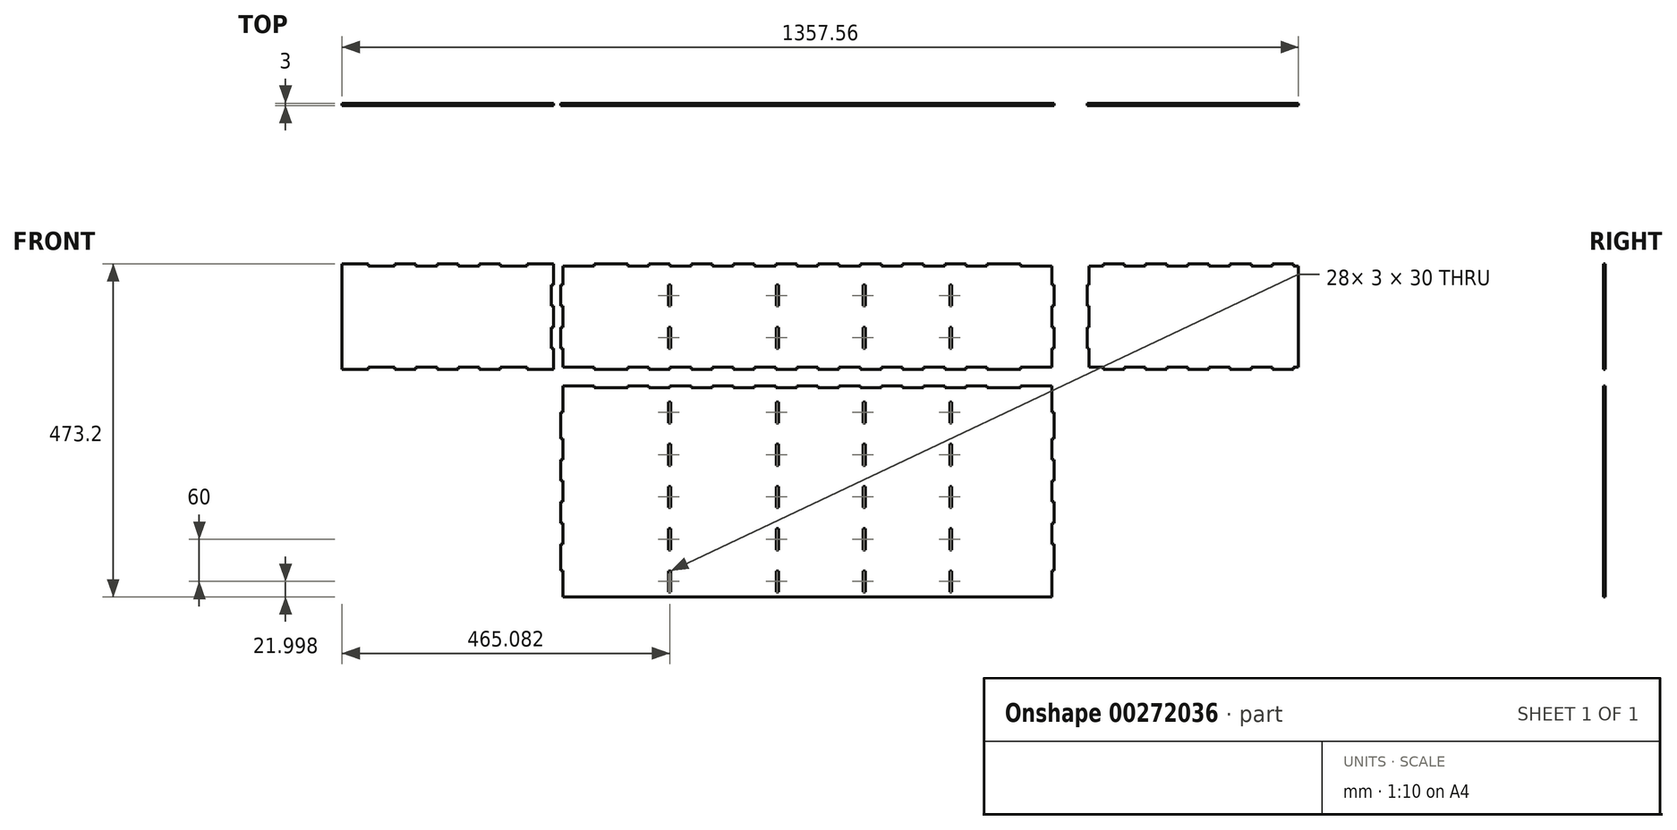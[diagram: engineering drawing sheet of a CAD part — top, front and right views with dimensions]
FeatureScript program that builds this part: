
annotation { "Feature Type Name" : "Feature", "Feature Type Description" : "" }
export const myFeature = defineFeature(function(context is Context, id is Id, definition is map)
    precondition{}
    {
        {
            var Q0;
            Q0=qCreatedBy(makeId("Front.planeOp"),FACE);
            var sketch = newSketch(context, id + "F0", { "sketchPlane" : qUnion([Q0])});
            skLineSegment(sketch, "E0", {"start": v(-505.3, 86.6) * mm, "end": v(-505.3, 116.6) * mm});
            skLineSegment(sketch, "E1", {"start": v(-505.3, 116.6) * mm, "end": v(-502.3, 116.6) * mm});
            skLineSegment(sketch, "E2", {"start": v(-502.3, 116.6) * mm, "end": v(-502.3, 146.6) * mm});
            skLineSegment(sketch, "E3", {"start": v(-502.3, 146.6) * mm, "end": v(-505.3, 146.6) * mm});
            skLineSegment(sketch, "E4", {"start": v(-505.3, 146.6) * mm, "end": v(-505.3, 176.6) * mm});
            skLineSegment(sketch, "E5", {"start": v(-505.3, 176.6) * mm, "end": v(-502.3, 176.6) * mm});
            skLineSegment(sketch, "E6", {"start": v(-502.3, 176.6) * mm, "end": v(-502.3, 206.6) * mm});
            skLineSegment(sketch, "E7", {"start": v(-502.3, 206.6) * mm, "end": v(-505.3, 206.6) * mm});
            skLineSegment(sketch, "E8", {"start": v(-505.3, 206.6) * mm, "end": v(-505.3, 236.6) * mm});
            skLineSegment(sketch, "E9", {"start": v(-505.3, 236.6) * mm, "end": v(-467.8, 236.6) * mm});
            skLineSegment(sketch, "E10", {"start": v(-467.8, 236.6) * mm, "end": v(-467.8, 233.6) * mm});
            skLineSegment(sketch, "E11", {"start": v(-467.8, 233.6) * mm, "end": v(-430.3, 233.6) * mm});
            skLineSegment(sketch, "E12", {"start": v(-430.3, 233.6) * mm, "end": v(-430.3, 236.6) * mm});
            skLineSegment(sketch, "E13", {"start": v(-430.3, 236.6) * mm, "end": v(-400.3, 236.6) * mm});
            skLineSegment(sketch, "E14", {"start": v(-400.3, 236.6) * mm, "end": v(-400.3, 233.6) * mm});
            skLineSegment(sketch, "E15", {"start": v(-400.3, 233.6) * mm, "end": v(-370.3, 233.6) * mm});
            skLineSegment(sketch, "E16", {"start": v(-370.3, 233.6) * mm, "end": v(-370.3, 236.6) * mm});
            skLineSegment(sketch, "E17", {"start": v(-370.3, 236.6) * mm, "end": v(-340.3, 236.6) * mm});
            skLineSegment(sketch, "E18", {"start": v(-340.3, 236.6) * mm, "end": v(-340.3, 233.6) * mm});
            skLineSegment(sketch, "E19", {"start": v(-340.3, 233.6) * mm, "end": v(-310.3, 233.6) * mm});
            skLineSegment(sketch, "E20", {"start": v(-310.3, 233.6) * mm, "end": v(-310.3, 236.6) * mm});
            skLineSegment(sketch, "E21", {"start": v(-310.3, 236.6) * mm, "end": v(-280.3, 236.6) * mm});
            skLineSegment(sketch, "E22", {"start": v(-280.3, 236.6) * mm, "end": v(-280.3, 233.6) * mm});
            skLineSegment(sketch, "E23", {"start": v(-280.3, 233.6) * mm, "end": v(-242.8, 233.6) * mm});
            skLineSegment(sketch, "E24", {"start": v(-242.8, 233.6) * mm, "end": v(-242.8, 236.6) * mm});
            skLineSegment(sketch, "E25", {"start": v(-242.8, 236.6) * mm, "end": v(-205.3, 236.6) * mm});
            skLineSegment(sketch, "E26", {"start": v(-205.3, 236.6) * mm, "end": v(-205.3, 206.6) * mm});
            skLineSegment(sketch, "E27", {"start": v(-205.3, 206.6) * mm, "end": v(-208.3, 206.6) * mm});
            skLineSegment(sketch, "E28", {"start": v(-208.3, 206.6) * mm, "end": v(-208.3, 176.6) * mm});
            skLineSegment(sketch, "E29", {"start": v(-208.3, 176.6) * mm, "end": v(-205.3, 176.6) * mm});
            skLineSegment(sketch, "E30", {"start": v(-205.3, 176.6) * mm, "end": v(-205.3, 146.6) * mm});
            skLineSegment(sketch, "E31", {"start": v(-205.3, 146.6) * mm, "end": v(-208.3, 146.6) * mm});
            skLineSegment(sketch, "E32", {"start": v(-208.3, 146.6) * mm, "end": v(-208.3, 116.6) * mm});
            skLineSegment(sketch, "E33", {"start": v(-208.3, 116.6) * mm, "end": v(-205.3, 116.6) * mm});
            skLineSegment(sketch, "E34", {"start": v(-205.3, 116.6) * mm, "end": v(-205.3, 86.6) * mm});
            skLineSegment(sketch, "E35", {"start": v(-205.3, 86.6) * mm, "end": v(-242.8, 86.6) * mm});
            skLineSegment(sketch, "E36", {"start": v(-242.8, 86.6) * mm, "end": v(-242.8, 89.6) * mm});
            skLineSegment(sketch, "E37", {"start": v(-242.8, 89.6) * mm, "end": v(-280.3, 89.6) * mm});
            skLineSegment(sketch, "E38", {"start": v(-280.3, 89.6) * mm, "end": v(-280.3, 86.6) * mm});
            skLineSegment(sketch, "E39", {"start": v(-280.3, 86.6) * mm, "end": v(-310.3, 86.6) * mm});
            skLineSegment(sketch, "E40", {"start": v(-310.3, 86.6) * mm, "end": v(-310.3, 89.6) * mm});
            skLineSegment(sketch, "E41", {"start": v(-310.3, 89.6) * mm, "end": v(-340.3, 89.6) * mm});
            skLineSegment(sketch, "E42", {"start": v(-340.3, 89.6) * mm, "end": v(-340.3, 86.6) * mm});
            skLineSegment(sketch, "E43", {"start": v(-340.3, 86.6) * mm, "end": v(-370.3, 86.6) * mm});
            skLineSegment(sketch, "E44", {"start": v(-370.3, 86.6) * mm, "end": v(-370.3, 89.6) * mm});
            skLineSegment(sketch, "E45", {"start": v(-370.3, 89.6) * mm, "end": v(-400.3, 89.6) * mm});
            skLineSegment(sketch, "E46", {"start": v(-400.3, 89.6) * mm, "end": v(-400.3, 86.6) * mm});
            skLineSegment(sketch, "E47", {"start": v(-400.3, 86.6) * mm, "end": v(-430.3, 86.6) * mm});
            skLineSegment(sketch, "E48", {"start": v(-430.3, 86.6) * mm, "end": v(-430.3, 89.6) * mm});
            skLineSegment(sketch, "E49", {"start": v(-430.3, 89.6) * mm, "end": v(-467.8, 89.6) * mm});
            skLineSegment(sketch, "E50", {"start": v(-467.8, 89.6) * mm, "end": v(-467.8, 86.6) * mm});
            skLineSegment(sketch, "E51", {"start": v(-467.8, 86.6) * mm, "end": v(-505.3, 86.6) * mm});
            skLineSegment(sketch, "E52", {"start": v(-191.7, 63.4) * mm, "end": v(-147.2, 63.4) * mm});
            skLineSegment(sketch, "E53", {"start": v(-147.2, 63.4) * mm, "end": v(-147.2, 60.4) * mm});
            skLineSegment(sketch, "E54", {"start": v(-147.2, 60.4) * mm, "end": v(-99.7, 60.4) * mm});
            skLineSegment(sketch, "E55", {"start": v(-99.7, 60.4) * mm, "end": v(-99.7, 63.4) * mm});
            skLineSegment(sketch, "E56", {"start": v(-99.7, 63.4) * mm, "end": v(-69.7, 63.4) * mm});
            skLineSegment(sketch, "E57", {"start": v(-69.7, 63.4) * mm, "end": v(-69.7, 60.4) * mm});
            skLineSegment(sketch, "E58", {"start": v(-69.7, 60.4) * mm, "end": v(-39.7, 60.4) * mm});
            skLineSegment(sketch, "E59", {"start": v(-39.7, 60.4) * mm, "end": v(-39.7, 63.4) * mm});
            skLineSegment(sketch, "E60", {"start": v(-39.7, 63.4) * mm, "end": v(-9.7, 63.4) * mm});
            skLineSegment(sketch, "E61", {"start": v(-9.7, 63.4) * mm, "end": v(-9.7, 60.4) * mm});
            skLineSegment(sketch, "E62", {"start": v(-9.7, 60.4) * mm, "end": v(20.3, 60.4) * mm});
            skLineSegment(sketch, "E63", {"start": v(20.3, 60.4) * mm, "end": v(20.3, 63.4) * mm});
            skLineSegment(sketch, "E64", {"start": v(20.3, 63.4) * mm, "end": v(50.3, 63.4) * mm});
            skLineSegment(sketch, "E65", {"start": v(50.3, 63.4) * mm, "end": v(50.3, 60.4) * mm});
            skLineSegment(sketch, "E66", {"start": v(50.3, 60.4) * mm, "end": v(80.3, 60.4) * mm});
            skLineSegment(sketch, "E67", {"start": v(80.3, 60.4) * mm, "end": v(80.3, 63.4) * mm});
            skLineSegment(sketch, "E68", {"start": v(80.3, 63.4) * mm, "end": v(110.3, 63.4) * mm});
            skLineSegment(sketch, "E69", {"start": v(110.3, 63.4) * mm, "end": v(110.3, 60.4) * mm});
            skLineSegment(sketch, "E70", {"start": v(110.3, 60.4) * mm, "end": v(140.3, 60.4) * mm});
            skLineSegment(sketch, "E71", {"start": v(140.3, 60.4) * mm, "end": v(140.3, 63.4) * mm});
            skLineSegment(sketch, "E72", {"start": v(140.3, 63.4) * mm, "end": v(170.3, 63.4) * mm});
            skLineSegment(sketch, "E73", {"start": v(170.3, 63.4) * mm, "end": v(170.3, 60.4) * mm});
            skLineSegment(sketch, "E74", {"start": v(170.3, 60.4) * mm, "end": v(200.3, 60.4) * mm});
            skLineSegment(sketch, "E75", {"start": v(200.3, 60.4) * mm, "end": v(200.3, 63.4) * mm});
            skLineSegment(sketch, "E76", {"start": v(200.3, 63.4) * mm, "end": v(230.3, 63.4) * mm});
            skLineSegment(sketch, "E77", {"start": v(230.3, 63.4) * mm, "end": v(230.3, 60.4) * mm});
            skLineSegment(sketch, "E78", {"start": v(230.3, 60.4) * mm, "end": v(260.3, 60.4) * mm});
            skLineSegment(sketch, "E79", {"start": v(260.3, 60.4) * mm, "end": v(260.3, 63.4) * mm});
            skLineSegment(sketch, "E80", {"start": v(260.3, 63.4) * mm, "end": v(290.3, 63.4) * mm});
            skLineSegment(sketch, "E81", {"start": v(290.3, 63.4) * mm, "end": v(290.3, 60.4) * mm});
            skLineSegment(sketch, "E82", {"start": v(290.3, 60.4) * mm, "end": v(320.3, 60.4) * mm});
            skLineSegment(sketch, "E83", {"start": v(320.3, 60.4) * mm, "end": v(320.3, 63.4) * mm});
            skLineSegment(sketch, "E84", {"start": v(320.3, 63.4) * mm, "end": v(350.3, 63.4) * mm});
            skLineSegment(sketch, "E85", {"start": v(350.3, 63.4) * mm, "end": v(350.3, 60.4) * mm});
            skLineSegment(sketch, "E86", {"start": v(350.3, 60.4) * mm, "end": v(380.3, 60.4) * mm});
            skLineSegment(sketch, "E87", {"start": v(380.3, 60.4) * mm, "end": v(380.3, 63.4) * mm});
            skLineSegment(sketch, "E88", {"start": v(380.3, 63.4) * mm, "end": v(410.3, 63.4) * mm});
            skLineSegment(sketch, "E89", {"start": v(410.3, 63.4) * mm, "end": v(410.3, 60.4) * mm});
            skLineSegment(sketch, "E90", {"start": v(410.3, 60.4) * mm, "end": v(457.8, 60.4) * mm});
            skLineSegment(sketch, "E91", {"start": v(457.8, 60.4) * mm, "end": v(457.8, 63.4) * mm});
            skLineSegment(sketch, "E92", {"start": v(457.8, 63.4) * mm, "end": v(502.3, 63.4) * mm});
            skLineSegment(sketch, "E93", {"start": v(502.3, 63.4) * mm, "end": v(502.3, 25.9) * mm});
            skLineSegment(sketch, "E94", {"start": v(502.3, 25.9) * mm, "end": v(505.3, 25.9) * mm});
            skLineSegment(sketch, "E95", {"start": v(505.3, 25.9) * mm, "end": v(505.3, -11.6) * mm});
            skLineSegment(sketch, "E96", {"start": v(505.3, -11.6) * mm, "end": v(502.3, -11.6) * mm});
            skLineSegment(sketch, "E97", {"start": v(502.3, -11.6) * mm, "end": v(502.3, -41.6) * mm});
            skLineSegment(sketch, "E98", {"start": v(502.3, -41.6) * mm, "end": v(505.3, -41.6) * mm});
            skLineSegment(sketch, "E99", {"start": v(505.3, -41.6) * mm, "end": v(505.3, -71.6) * mm});
            skLineSegment(sketch, "E100", {"start": v(505.3, -71.6) * mm, "end": v(502.3, -71.6) * mm});
            skLineSegment(sketch, "E101", {"start": v(502.3, -71.6) * mm, "end": v(502.3, -101.6) * mm});
            skLineSegment(sketch, "E102", {"start": v(502.3, -101.6) * mm, "end": v(505.3, -101.6) * mm});
            skLineSegment(sketch, "E103", {"start": v(505.3, -101.6) * mm, "end": v(505.3, -131.6) * mm});
            skLineSegment(sketch, "E104", {"start": v(505.3, -131.6) * mm, "end": v(502.3, -131.6) * mm});
            skLineSegment(sketch, "E105", {"start": v(502.3, -131.6) * mm, "end": v(502.3, -161.6) * mm});
            skLineSegment(sketch, "E106", {"start": v(502.3, -161.6) * mm, "end": v(505.3, -161.6) * mm});
            skLineSegment(sketch, "E107", {"start": v(505.3, -161.6) * mm, "end": v(505.3, -199.1) * mm});
            skLineSegment(sketch, "E108", {"start": v(505.3, -199.1) * mm, "end": v(502.3, -199.1) * mm});
            skLineSegment(sketch, "E109", {"start": v(502.3, -199.1) * mm, "end": v(502.3, -236.6) * mm});
            skLineSegment(sketch, "E110", {"start": v(502.3, -236.6) * mm, "end": v(457.8, -236.6) * mm});
            skLineSegment(sketch, "E111", {"start": v(457.8, -236.6) * mm, "end": v(457.8, -233.6) * mm});
            skLineSegment(sketch, "E112", {"start": v(457.8, -233.6) * mm, "end": v(410.3, -233.6) * mm});
            skLineSegment(sketch, "E113", {"start": v(410.3, -233.6) * mm, "end": v(410.3, -236.6) * mm});
            skLineSegment(sketch, "E114", {"start": v(410.3, -236.6) * mm, "end": v(380.3, -236.6) * mm});
            skLineSegment(sketch, "E115", {"start": v(380.3, -236.6) * mm, "end": v(380.3, -233.6) * mm});
            skLineSegment(sketch, "E116", {"start": v(380.3, -233.6) * mm, "end": v(350.3, -233.6) * mm});
            skLineSegment(sketch, "E117", {"start": v(350.3, -233.6) * mm, "end": v(350.3, -236.6) * mm});
            skLineSegment(sketch, "E118", {"start": v(350.3, -236.6) * mm, "end": v(320.3, -236.6) * mm});
            skLineSegment(sketch, "E119", {"start": v(320.3, -236.6) * mm, "end": v(320.3, -233.6) * mm});
            skLineSegment(sketch, "E120", {"start": v(320.3, -233.6) * mm, "end": v(290.3, -233.6) * mm});
            skLineSegment(sketch, "E121", {"start": v(290.3, -233.6) * mm, "end": v(290.3, -236.6) * mm});
            skLineSegment(sketch, "E122", {"start": v(290.3, -236.6) * mm, "end": v(260.3, -236.6) * mm});
            skLineSegment(sketch, "E123", {"start": v(260.3, -236.6) * mm, "end": v(260.3, -233.6) * mm});
            skLineSegment(sketch, "E124", {"start": v(260.3, -233.6) * mm, "end": v(230.3, -233.6) * mm});
            skLineSegment(sketch, "E125", {"start": v(230.3, -233.6) * mm, "end": v(230.3, -236.6) * mm});
            skLineSegment(sketch, "E126", {"start": v(230.3, -236.6) * mm, "end": v(200.3, -236.6) * mm});
            skLineSegment(sketch, "E127", {"start": v(200.3, -236.6) * mm, "end": v(200.3, -233.6) * mm});
            skLineSegment(sketch, "E128", {"start": v(200.3, -233.6) * mm, "end": v(170.3, -233.6) * mm});
            skLineSegment(sketch, "E129", {"start": v(170.3, -233.6) * mm, "end": v(170.3, -236.6) * mm});
            skLineSegment(sketch, "E130", {"start": v(170.3, -236.6) * mm, "end": v(140.3, -236.6) * mm});
            skLineSegment(sketch, "E131", {"start": v(140.3, -236.6) * mm, "end": v(140.3, -233.6) * mm});
            skLineSegment(sketch, "E132", {"start": v(140.3, -233.6) * mm, "end": v(110.3, -233.6) * mm});
            skLineSegment(sketch, "E133", {"start": v(110.3, -233.6) * mm, "end": v(110.3, -236.6) * mm});
            skLineSegment(sketch, "E134", {"start": v(110.3, -236.6) * mm, "end": v(80.3, -236.6) * mm});
            skLineSegment(sketch, "E135", {"start": v(80.3, -236.6) * mm, "end": v(80.3, -233.6) * mm});
            skLineSegment(sketch, "E136", {"start": v(80.3, -233.6) * mm, "end": v(50.3, -233.6) * mm});
            skLineSegment(sketch, "E137", {"start": v(50.3, -233.6) * mm, "end": v(50.3, -236.6) * mm});
            skLineSegment(sketch, "E138", {"start": v(50.3, -236.6) * mm, "end": v(20.3, -236.6) * mm});
            skLineSegment(sketch, "E139", {"start": v(20.3, -236.6) * mm, "end": v(20.3, -233.6) * mm});
            skLineSegment(sketch, "E140", {"start": v(20.3, -233.6) * mm, "end": v(-9.7, -233.6) * mm});
            skLineSegment(sketch, "E141", {"start": v(-9.7, -233.6) * mm, "end": v(-9.7, -236.6) * mm});
            skLineSegment(sketch, "E142", {"start": v(-9.7, -236.6) * mm, "end": v(-39.7, -236.6) * mm});
            skLineSegment(sketch, "E143", {"start": v(-39.7, -236.6) * mm, "end": v(-39.7, -233.6) * mm});
            skLineSegment(sketch, "E144", {"start": v(-39.7, -233.6) * mm, "end": v(-69.7, -233.6) * mm});
            skLineSegment(sketch, "E145", {"start": v(-69.7, -233.6) * mm, "end": v(-69.7, -236.6) * mm});
            skLineSegment(sketch, "E146", {"start": v(-69.7, -236.6) * mm, "end": v(-99.7, -236.6) * mm});
            skLineSegment(sketch, "E147", {"start": v(-99.7, -236.6) * mm, "end": v(-99.7, -233.6) * mm});
            skLineSegment(sketch, "E148", {"start": v(-99.7, -233.6) * mm, "end": v(-147.2, -233.6) * mm});
            skLineSegment(sketch, "E149", {"start": v(-147.2, -233.6) * mm, "end": v(-147.2, -236.6) * mm});
            skLineSegment(sketch, "E150", {"start": v(-147.2, -236.6) * mm, "end": v(-191.7, -236.6) * mm});
            skLineSegment(sketch, "E151", {"start": v(-191.7, -236.6) * mm, "end": v(-191.7, -199.1) * mm});
            skLineSegment(sketch, "E152", {"start": v(-191.7, -199.1) * mm, "end": v(-194.7, -199.1) * mm});
            skLineSegment(sketch, "E153", {"start": v(-194.7, -199.1) * mm, "end": v(-194.7, -161.6) * mm});
            skLineSegment(sketch, "E154", {"start": v(-194.7, -161.6) * mm, "end": v(-191.7, -161.6) * mm});
            skLineSegment(sketch, "E155", {"start": v(-191.7, -161.6) * mm, "end": v(-191.7, -131.6) * mm});
            skLineSegment(sketch, "E156", {"start": v(-191.7, -131.6) * mm, "end": v(-194.7, -131.6) * mm});
            skLineSegment(sketch, "E157", {"start": v(-194.7, -131.6) * mm, "end": v(-194.7, -101.6) * mm});
            skLineSegment(sketch, "E158", {"start": v(-194.7, -101.6) * mm, "end": v(-191.7, -101.6) * mm});
            skLineSegment(sketch, "E159", {"start": v(-191.7, -101.6) * mm, "end": v(-191.7, -71.6) * mm});
            skLineSegment(sketch, "E160", {"start": v(-191.7, -71.6) * mm, "end": v(-194.7, -71.6) * mm});
            skLineSegment(sketch, "E161", {"start": v(-194.7, -71.6) * mm, "end": v(-194.7, -41.6) * mm});
            skLineSegment(sketch, "E162", {"start": v(-194.7, -41.6) * mm, "end": v(-191.7, -41.6) * mm});
            skLineSegment(sketch, "E163", {"start": v(-191.7, -41.6) * mm, "end": v(-191.7, -11.6) * mm});
            skLineSegment(sketch, "E164", {"start": v(-191.7, -11.6) * mm, "end": v(-194.7, -11.6) * mm});
            skLineSegment(sketch, "E165", {"start": v(-194.7, -11.6) * mm, "end": v(-194.7, 25.9) * mm});
            skLineSegment(sketch, "E166", {"start": v(-194.7, 25.9) * mm, "end": v(-191.7, 25.9) * mm});
            skLineSegment(sketch, "E167", {"start": v(-191.7, 25.9) * mm, "end": v(-191.7, 63.4) * mm});
            skLineSegment(sketch, "E168", {"start": v(502.3, 233.6) * mm, "end": v(502.3, 206.6) * mm});
            skLineSegment(sketch, "E169", {"start": v(502.3, 206.6) * mm, "end": v(505.3, 206.6) * mm});
            skLineSegment(sketch, "E170", {"start": v(505.3, 206.6) * mm, "end": v(505.3, 176.6) * mm});
            skLineSegment(sketch, "E171", {"start": v(505.3, 176.6) * mm, "end": v(502.3, 176.6) * mm});
            skLineSegment(sketch, "E172", {"start": v(502.3, 176.6) * mm, "end": v(502.3, 146.6) * mm});
            skLineSegment(sketch, "E173", {"start": v(502.3, 146.6) * mm, "end": v(505.3, 146.6) * mm});
            skLineSegment(sketch, "E174", {"start": v(505.3, 146.6) * mm, "end": v(505.3, 116.6) * mm});
            skLineSegment(sketch, "E175", {"start": v(505.3, 116.6) * mm, "end": v(502.3, 116.6) * mm});
            skLineSegment(sketch, "E176", {"start": v(502.3, 116.6) * mm, "end": v(502.3, 89.6) * mm});
            skLineSegment(sketch, "E177", {"start": v(502.3, 89.6) * mm, "end": v(457.8, 89.6) * mm});
            skLineSegment(sketch, "E178", {"start": v(457.8, 89.6) * mm, "end": v(457.8, 86.6) * mm});
            skLineSegment(sketch, "E179", {"start": v(457.8, 86.6) * mm, "end": v(410.3, 86.6) * mm});
            skLineSegment(sketch, "E180", {"start": v(410.3, 86.6) * mm, "end": v(410.3, 89.6) * mm});
            skLineSegment(sketch, "E181", {"start": v(410.3, 89.6) * mm, "end": v(380.3, 89.6) * mm});
            skLineSegment(sketch, "E182", {"start": v(380.3, 89.6) * mm, "end": v(380.3, 86.6) * mm});
            skLineSegment(sketch, "E183", {"start": v(380.3, 86.6) * mm, "end": v(350.3, 86.6) * mm});
            skLineSegment(sketch, "E184", {"start": v(350.3, 86.6) * mm, "end": v(350.3, 89.6) * mm});
            skLineSegment(sketch, "E185", {"start": v(350.3, 89.6) * mm, "end": v(320.3, 89.6) * mm});
            skLineSegment(sketch, "E186", {"start": v(320.3, 89.6) * mm, "end": v(320.3, 86.6) * mm});
            skLineSegment(sketch, "E187", {"start": v(320.3, 86.6) * mm, "end": v(290.3, 86.6) * mm});
            skLineSegment(sketch, "E188", {"start": v(290.3, 86.6) * mm, "end": v(290.3, 89.6) * mm});
            skLineSegment(sketch, "E189", {"start": v(290.3, 89.6) * mm, "end": v(260.3, 89.6) * mm});
            skLineSegment(sketch, "E190", {"start": v(260.3, 89.6) * mm, "end": v(260.3, 86.6) * mm});
            skLineSegment(sketch, "E191", {"start": v(260.3, 86.6) * mm, "end": v(230.3, 86.6) * mm});
            skLineSegment(sketch, "E192", {"start": v(230.3, 86.6) * mm, "end": v(230.3, 89.6) * mm});
            skLineSegment(sketch, "E193", {"start": v(230.3, 89.6) * mm, "end": v(200.3, 89.6) * mm});
            skLineSegment(sketch, "E194", {"start": v(200.3, 89.6) * mm, "end": v(200.3, 86.6) * mm});
            skLineSegment(sketch, "E195", {"start": v(200.3, 86.6) * mm, "end": v(170.3, 86.6) * mm});
            skLineSegment(sketch, "E196", {"start": v(170.3, 86.6) * mm, "end": v(170.3, 89.6) * mm});
            skLineSegment(sketch, "E197", {"start": v(170.3, 89.6) * mm, "end": v(140.3, 89.6) * mm});
            skLineSegment(sketch, "E198", {"start": v(140.3, 89.6) * mm, "end": v(140.3, 86.6) * mm});
            skLineSegment(sketch, "E199", {"start": v(140.3, 86.6) * mm, "end": v(110.3, 86.6) * mm});
            skLineSegment(sketch, "E200", {"start": v(110.3, 86.6) * mm, "end": v(110.3, 89.6) * mm});
            skLineSegment(sketch, "E201", {"start": v(110.3, 89.6) * mm, "end": v(80.3, 89.6) * mm});
            skLineSegment(sketch, "E202", {"start": v(80.3, 89.6) * mm, "end": v(80.3, 86.6) * mm});
            skLineSegment(sketch, "E203", {"start": v(80.3, 86.6) * mm, "end": v(50.3, 86.6) * mm});
            skLineSegment(sketch, "E204", {"start": v(50.3, 86.6) * mm, "end": v(50.3, 89.6) * mm});
            skLineSegment(sketch, "E205", {"start": v(50.3, 89.6) * mm, "end": v(20.3, 89.6) * mm});
            skLineSegment(sketch, "E206", {"start": v(20.3, 89.6) * mm, "end": v(20.3, 86.6) * mm});
            skLineSegment(sketch, "E207", {"start": v(20.3, 86.6) * mm, "end": v(-9.7, 86.6) * mm});
            skLineSegment(sketch, "E208", {"start": v(-9.7, 86.6) * mm, "end": v(-9.7, 89.6) * mm});
            skLineSegment(sketch, "E209", {"start": v(-9.7, 89.6) * mm, "end": v(-39.7, 89.6) * mm});
            skLineSegment(sketch, "E210", {"start": v(-39.7, 89.6) * mm, "end": v(-39.7, 86.6) * mm});
            skLineSegment(sketch, "E211", {"start": v(-39.7, 86.6) * mm, "end": v(-69.7, 86.6) * mm});
            skLineSegment(sketch, "E212", {"start": v(-69.7, 86.6) * mm, "end": v(-69.7, 89.6) * mm});
            skLineSegment(sketch, "E213", {"start": v(-69.7, 89.6) * mm, "end": v(-99.7, 89.6) * mm});
            skLineSegment(sketch, "E214", {"start": v(-99.7, 89.6) * mm, "end": v(-99.7, 86.6) * mm});
            skLineSegment(sketch, "E215", {"start": v(-99.7, 86.6) * mm, "end": v(-147.2, 86.6) * mm});
            skLineSegment(sketch, "E216", {"start": v(-147.2, 86.6) * mm, "end": v(-147.2, 89.6) * mm});
            skLineSegment(sketch, "E217", {"start": v(-147.2, 89.6) * mm, "end": v(-191.7, 89.6) * mm});
            skLineSegment(sketch, "E218", {"start": v(-191.7, 89.6) * mm, "end": v(-191.7, 116.6) * mm});
            skLineSegment(sketch, "E219", {"start": v(-191.7, 116.6) * mm, "end": v(-194.7, 116.6) * mm});
            skLineSegment(sketch, "E220", {"start": v(-194.7, 116.6) * mm, "end": v(-194.7, 146.6) * mm});
            skLineSegment(sketch, "E221", {"start": v(-194.7, 146.6) * mm, "end": v(-191.7, 146.6) * mm});
            skLineSegment(sketch, "E222", {"start": v(-191.7, 146.6) * mm, "end": v(-191.7, 176.6) * mm});
            skLineSegment(sketch, "E223", {"start": v(-191.7, 176.6) * mm, "end": v(-194.7, 176.6) * mm});
            skLineSegment(sketch, "E224", {"start": v(-194.7, 176.6) * mm, "end": v(-194.7, 206.6) * mm});
            skLineSegment(sketch, "E225", {"start": v(-194.7, 206.6) * mm, "end": v(-191.7, 206.6) * mm});
            skLineSegment(sketch, "E226", {"start": v(-191.7, 206.6) * mm, "end": v(-191.7, 233.6) * mm});
            skLineSegment(sketch, "E227", {"start": v(-191.7, 233.6) * mm, "end": v(-147.2, 233.6) * mm});
            skLineSegment(sketch, "E228", {"start": v(-147.2, 233.6) * mm, "end": v(-147.2, 236.6) * mm});
            skLineSegment(sketch, "E229", {"start": v(-147.2, 236.6) * mm, "end": v(-99.7, 236.6) * mm});
            skLineSegment(sketch, "E230", {"start": v(-99.7, 236.6) * mm, "end": v(-99.7, 233.6) * mm});
            skLineSegment(sketch, "E231", {"start": v(-99.7, 233.6) * mm, "end": v(-69.7, 233.6) * mm});
            skLineSegment(sketch, "E232", {"start": v(-69.7, 233.6) * mm, "end": v(-69.7, 236.6) * mm});
            skLineSegment(sketch, "E233", {"start": v(-69.7, 236.6) * mm, "end": v(-39.7, 236.6) * mm});
            skLineSegment(sketch, "E234", {"start": v(-39.7, 236.6) * mm, "end": v(-39.7, 233.6) * mm});
            skLineSegment(sketch, "E235", {"start": v(-39.7, 233.6) * mm, "end": v(-9.7, 233.6) * mm});
            skLineSegment(sketch, "E236", {"start": v(-9.7, 233.6) * mm, "end": v(-9.7, 236.6) * mm});
            skLineSegment(sketch, "E237", {"start": v(-9.7, 236.6) * mm, "end": v(20.3, 236.6) * mm});
            skLineSegment(sketch, "E238", {"start": v(20.3, 236.6) * mm, "end": v(20.3, 233.6) * mm});
            skLineSegment(sketch, "E239", {"start": v(20.3, 233.6) * mm, "end": v(50.3, 233.6) * mm});
            skLineSegment(sketch, "E240", {"start": v(50.3, 233.6) * mm, "end": v(50.3, 236.6) * mm});
            skLineSegment(sketch, "E241", {"start": v(50.3, 236.6) * mm, "end": v(80.3, 236.6) * mm});
            skLineSegment(sketch, "E242", {"start": v(80.3, 236.6) * mm, "end": v(80.3, 233.6) * mm});
            skLineSegment(sketch, "E243", {"start": v(80.3, 233.6) * mm, "end": v(110.3, 233.6) * mm});
            skLineSegment(sketch, "E244", {"start": v(110.3, 233.6) * mm, "end": v(110.3, 236.6) * mm});
            skLineSegment(sketch, "E245", {"start": v(110.3, 236.6) * mm, "end": v(140.3, 236.6) * mm});
            skLineSegment(sketch, "E246", {"start": v(140.3, 236.6) * mm, "end": v(140.3, 233.6) * mm});
            skLineSegment(sketch, "E247", {"start": v(140.3, 233.6) * mm, "end": v(170.3, 233.6) * mm});
            skLineSegment(sketch, "E248", {"start": v(170.3, 233.6) * mm, "end": v(170.3, 236.6) * mm});
            skLineSegment(sketch, "E249", {"start": v(170.3, 236.6) * mm, "end": v(200.3, 236.6) * mm});
            skLineSegment(sketch, "E250", {"start": v(200.3, 236.6) * mm, "end": v(200.3, 233.6) * mm});
            skLineSegment(sketch, "E251", {"start": v(200.3, 233.6) * mm, "end": v(230.3, 233.6) * mm});
            skLineSegment(sketch, "E252", {"start": v(230.3, 233.6) * mm, "end": v(230.3, 236.6) * mm});
            skLineSegment(sketch, "E253", {"start": v(230.3, 236.6) * mm, "end": v(260.3, 236.6) * mm});
            skLineSegment(sketch, "E254", {"start": v(260.3, 236.6) * mm, "end": v(260.3, 233.6) * mm});
            skLineSegment(sketch, "E255", {"start": v(260.3, 233.6) * mm, "end": v(290.3, 233.6) * mm});
            skLineSegment(sketch, "E256", {"start": v(290.3, 233.6) * mm, "end": v(290.3, 236.6) * mm});
            skLineSegment(sketch, "E257", {"start": v(290.3, 236.6) * mm, "end": v(320.3, 236.6) * mm});
            skLineSegment(sketch, "E258", {"start": v(320.3, 236.6) * mm, "end": v(320.3, 233.6) * mm});
            skLineSegment(sketch, "E259", {"start": v(320.3, 233.6) * mm, "end": v(350.3, 233.6) * mm});
            skLineSegment(sketch, "E260", {"start": v(350.3, 233.6) * mm, "end": v(350.3, 236.6) * mm});
            skLineSegment(sketch, "E261", {"start": v(350.3, 236.6) * mm, "end": v(380.3, 236.6) * mm});
            skLineSegment(sketch, "E262", {"start": v(380.3, 236.6) * mm, "end": v(380.3, 233.6) * mm});
            skLineSegment(sketch, "E263", {"start": v(380.3, 233.6) * mm, "end": v(410.3, 233.6) * mm});
            skLineSegment(sketch, "E264", {"start": v(410.3, 233.6) * mm, "end": v(410.3, 236.6) * mm});
            skLineSegment(sketch, "E265", {"start": v(410.3, 236.6) * mm, "end": v(457.8, 236.6) * mm});
            skLineSegment(sketch, "E266", {"start": v(457.8, 236.6) * mm, "end": v(457.8, 233.6) * mm});
            skLineSegment(sketch, "E267", {"start": v(457.8, 233.6) * mm, "end": v(502.3, 233.6) * mm});
            skSolve(sketch);
        }
        {
            var Q0;
            Q0 = qSketchRegion(id + "F0", true);
            extrude(context, id + "F1", {"entities" : qUnion([Q0]), "depth" : 3 * mm});
        }
        {
            var Q0;
            Q0=makeQuery(id+"F1.opExtrude","CAP_FACE",FACE,{"disambiguationData":[OSD([sQuery(id+"F0.wireOp",EDGE,"E52"),sQuery(id+"F0.wireOp",EDGE,"E53"),sQuery(id+"F0.wireOp",EDGE,"E54"),sQuery(id+"F0.wireOp",EDGE,"E55"),sQuery(id+"F0.wireOp",EDGE,"E56"),sQuery(id+"F0.wireOp",EDGE,"E57"),sQuery(id+"F0.wireOp",EDGE,"E58"),sQuery(id+"F0.wireOp",EDGE,"E59"),sQuery(id+"F0.wireOp",EDGE,"E60"),sQuery(id+"F0.wireOp",EDGE,"E61"),sQuery(id+"F0.wireOp",EDGE,"E62"),sQuery(id+"F0.wireOp",EDGE,"E63"),sQuery(id+"F0.wireOp",EDGE,"E64"),sQuery(id+"F0.wireOp",EDGE,"E65"),sQuery(id+"F0.wireOp",EDGE,"E66"),sQuery(id+"F0.wireOp",EDGE,"E67"),sQuery(id+"F0.wireOp",EDGE,"E68"),sQuery(id+"F0.wireOp",EDGE,"E69"),sQuery(id+"F0.wireOp",EDGE,"E70"),sQuery(id+"F0.wireOp",EDGE,"E71"),sQuery(id+"F0.wireOp",EDGE,"E72"),sQuery(id+"F0.wireOp",EDGE,"E73"),sQuery(id+"F0.wireOp",EDGE,"E74"),sQuery(id+"F0.wireOp",EDGE,"E75"),sQuery(id+"F0.wireOp",EDGE,"E76"),sQuery(id+"F0.wireOp",EDGE,"E77"),sQuery(id+"F0.wireOp",EDGE,"E78"),sQuery(id+"F0.wireOp",EDGE,"E79"),sQuery(id+"F0.wireOp",EDGE,"E80"),sQuery(id+"F0.wireOp",EDGE,"E81"),sQuery(id+"F0.wireOp",EDGE,"E82"),sQuery(id+"F0.wireOp",EDGE,"E83"),sQuery(id+"F0.wireOp",EDGE,"E84"),sQuery(id+"F0.wireOp",EDGE,"E85"),sQuery(id+"F0.wireOp",EDGE,"E86"),sQuery(id+"F0.wireOp",EDGE,"E87"),sQuery(id+"F0.wireOp",EDGE,"E88"),sQuery(id+"F0.wireOp",EDGE,"E89"),sQuery(id+"F0.wireOp",EDGE,"E90"),sQuery(id+"F0.wireOp",EDGE,"E91"),sQuery(id+"F0.wireOp",EDGE,"E92"),sQuery(id+"F0.wireOp",EDGE,"E93"),sQuery(id+"F0.wireOp",EDGE,"E94"),sQuery(id+"F0.wireOp",EDGE,"E95"),sQuery(id+"F0.wireOp",EDGE,"E96"),sQuery(id+"F0.wireOp",EDGE,"E97"),sQuery(id+"F0.wireOp",EDGE,"E98"),sQuery(id+"F0.wireOp",EDGE,"E99"),sQuery(id+"F0.wireOp",EDGE,"E100"),sQuery(id+"F0.wireOp",EDGE,"E101"),sQuery(id+"F0.wireOp",EDGE,"E102"),sQuery(id+"F0.wireOp",EDGE,"E103"),sQuery(id+"F0.wireOp",EDGE,"E104"),sQuery(id+"F0.wireOp",EDGE,"E105"),sQuery(id+"F0.wireOp",EDGE,"E106"),sQuery(id+"F0.wireOp",EDGE,"E107"),sQuery(id+"F0.wireOp",EDGE,"E108"),sQuery(id+"F0.wireOp",EDGE,"E109"),sQuery(id+"F0.wireOp",EDGE,"E110"),sQuery(id+"F0.wireOp",EDGE,"E111"),sQuery(id+"F0.wireOp",EDGE,"E112"),sQuery(id+"F0.wireOp",EDGE,"E113"),sQuery(id+"F0.wireOp",EDGE,"E114"),sQuery(id+"F0.wireOp",EDGE,"E115"),sQuery(id+"F0.wireOp",EDGE,"E116"),sQuery(id+"F0.wireOp",EDGE,"E117"),sQuery(id+"F0.wireOp",EDGE,"E118"),sQuery(id+"F0.wireOp",EDGE,"E119"),sQuery(id+"F0.wireOp",EDGE,"E120"),sQuery(id+"F0.wireOp",EDGE,"E121"),sQuery(id+"F0.wireOp",EDGE,"E122"),sQuery(id+"F0.wireOp",EDGE,"E123"),sQuery(id+"F0.wireOp",EDGE,"E124"),sQuery(id+"F0.wireOp",EDGE,"E125"),sQuery(id+"F0.wireOp",EDGE,"E126"),sQuery(id+"F0.wireOp",EDGE,"E127"),sQuery(id+"F0.wireOp",EDGE,"E128"),sQuery(id+"F0.wireOp",EDGE,"E129"),sQuery(id+"F0.wireOp",EDGE,"E130"),sQuery(id+"F0.wireOp",EDGE,"E131"),sQuery(id+"F0.wireOp",EDGE,"E132"),sQuery(id+"F0.wireOp",EDGE,"E133"),sQuery(id+"F0.wireOp",EDGE,"E134"),sQuery(id+"F0.wireOp",EDGE,"E135"),sQuery(id+"F0.wireOp",EDGE,"E136"),sQuery(id+"F0.wireOp",EDGE,"E137"),sQuery(id+"F0.wireOp",EDGE,"E138"),sQuery(id+"F0.wireOp",EDGE,"E139"),sQuery(id+"F0.wireOp",EDGE,"E140"),sQuery(id+"F0.wireOp",EDGE,"E141"),sQuery(id+"F0.wireOp",EDGE,"E142"),sQuery(id+"F0.wireOp",EDGE,"E143"),sQuery(id+"F0.wireOp",EDGE,"E144"),sQuery(id+"F0.wireOp",EDGE,"E145"),sQuery(id+"F0.wireOp",EDGE,"E146"),sQuery(id+"F0.wireOp",EDGE,"E147"),sQuery(id+"F0.wireOp",EDGE,"E148"),sQuery(id+"F0.wireOp",EDGE,"E149"),sQuery(id+"F0.wireOp",EDGE,"E150"),sQuery(id+"F0.wireOp",EDGE,"E151"),sQuery(id+"F0.wireOp",EDGE,"E152"),sQuery(id+"F0.wireOp",EDGE,"E153"),sQuery(id+"F0.wireOp",EDGE,"E154"),sQuery(id+"F0.wireOp",EDGE,"E155"),sQuery(id+"F0.wireOp",EDGE,"E156"),sQuery(id+"F0.wireOp",EDGE,"E157"),sQuery(id+"F0.wireOp",EDGE,"E158"),sQuery(id+"F0.wireOp",EDGE,"E159"),sQuery(id+"F0.wireOp",EDGE,"E160"),sQuery(id+"F0.wireOp",EDGE,"E161"),sQuery(id+"F0.wireOp",EDGE,"E162"),sQuery(id+"F0.wireOp",EDGE,"E163"),sQuery(id+"F0.wireOp",EDGE,"E164"),sQuery(id+"F0.wireOp",EDGE,"E165"),sQuery(id+"F0.wireOp",EDGE,"E166"),sQuery(id+"F0.wireOp",EDGE,"E167")])],"isStart":false});
            var sketch = newSketch(context, id + "F2", { "sketchPlane" : qUnion([Q0])});
            skLineSegment(sketch, "E268.bottom", {"start": v(-147.2, -236.6) * mm, "end": v(457.8, -236.6) * mm});
            skLineSegment(sketch, "E268.top", {"start": v(-147.2, -233.6) * mm, "end": v(457.8, -233.6) * mm});
            skLineSegment(sketch, "E268.left", {"start": v(-147.2, -236.6) * mm, "end": v(-147.2, -233.6) * mm});
            skLineSegment(sketch, "E268.right", {"start": v(457.8, -236.6) * mm, "end": v(457.8, -233.6) * mm});
            skSolve(sketch);
        }
        {
            var Q0;
            Q0 = qSketchRegion(id + "F2", true);
            extrude(context, id + "F3", {"entities" : qUnion([Q0]), "operationType" : NewBodyOperationType.ADD, "oppositeDirection" : true, "depth" : 3 * mm});
        }
        {
            var Q0;
            Q0=makeQuery(id+"F1.opExtrude","CAP_FACE",FACE,{"disambiguationData":[OSD([sQuery(id+"F0.wireOp",EDGE,"E0"),sQuery(id+"F0.wireOp",EDGE,"E1"),sQuery(id+"F0.wireOp",EDGE,"E2"),sQuery(id+"F0.wireOp",EDGE,"E3"),sQuery(id+"F0.wireOp",EDGE,"E4"),sQuery(id+"F0.wireOp",EDGE,"E5"),sQuery(id+"F0.wireOp",EDGE,"E6"),sQuery(id+"F0.wireOp",EDGE,"E7"),sQuery(id+"F0.wireOp",EDGE,"E8"),sQuery(id+"F0.wireOp",EDGE,"E9"),sQuery(id+"F0.wireOp",EDGE,"E10"),sQuery(id+"F0.wireOp",EDGE,"E11"),sQuery(id+"F0.wireOp",EDGE,"E12"),sQuery(id+"F0.wireOp",EDGE,"E13"),sQuery(id+"F0.wireOp",EDGE,"E14"),sQuery(id+"F0.wireOp",EDGE,"E15"),sQuery(id+"F0.wireOp",EDGE,"E16"),sQuery(id+"F0.wireOp",EDGE,"E17"),sQuery(id+"F0.wireOp",EDGE,"E18"),sQuery(id+"F0.wireOp",EDGE,"E19"),sQuery(id+"F0.wireOp",EDGE,"E20"),sQuery(id+"F0.wireOp",EDGE,"E21"),sQuery(id+"F0.wireOp",EDGE,"E22"),sQuery(id+"F0.wireOp",EDGE,"E23"),sQuery(id+"F0.wireOp",EDGE,"E24"),sQuery(id+"F0.wireOp",EDGE,"E25"),sQuery(id+"F0.wireOp",EDGE,"E26"),sQuery(id+"F0.wireOp",EDGE,"E27"),sQuery(id+"F0.wireOp",EDGE,"E28"),sQuery(id+"F0.wireOp",EDGE,"E29"),sQuery(id+"F0.wireOp",EDGE,"E30"),sQuery(id+"F0.wireOp",EDGE,"E31"),sQuery(id+"F0.wireOp",EDGE,"E32"),sQuery(id+"F0.wireOp",EDGE,"E33"),sQuery(id+"F0.wireOp",EDGE,"E34"),sQuery(id+"F0.wireOp",EDGE,"E35"),sQuery(id+"F0.wireOp",EDGE,"E36"),sQuery(id+"F0.wireOp",EDGE,"E37"),sQuery(id+"F0.wireOp",EDGE,"E38"),sQuery(id+"F0.wireOp",EDGE,"E39"),sQuery(id+"F0.wireOp",EDGE,"E40"),sQuery(id+"F0.wireOp",EDGE,"E41"),sQuery(id+"F0.wireOp",EDGE,"E42"),sQuery(id+"F0.wireOp",EDGE,"E43"),sQuery(id+"F0.wireOp",EDGE,"E44"),sQuery(id+"F0.wireOp",EDGE,"E45"),sQuery(id+"F0.wireOp",EDGE,"E46"),sQuery(id+"F0.wireOp",EDGE,"E47"),sQuery(id+"F0.wireOp",EDGE,"E48"),sQuery(id+"F0.wireOp",EDGE,"E49"),sQuery(id+"F0.wireOp",EDGE,"E50"),sQuery(id+"F0.wireOp",EDGE,"E51")])],"isStart":false});
            var sketch = newSketch(context, id + "F4", { "sketchPlane" : qUnion([Q0])});
            skLineSegment(sketch, "E269.bottom", {"start": v(-505.3, 206.6) * mm, "end": v(-502.3, 206.6) * mm});
            skLineSegment(sketch, "E269.top", {"start": v(-505.3, 116.6) * mm, "end": v(-502.3, 116.6) * mm});
            skLineSegment(sketch, "E269.left", {"start": v(-505.3, 206.6) * mm, "end": v(-505.3, 116.6) * mm});
            skLineSegment(sketch, "E269.right", {"start": v(-502.3, 206.6) * mm, "end": v(-502.3, 116.6) * mm});
            skSolve(sketch);
        }
        {
            var Q0;
            Q0 = qSketchRegion(id + "F4", true);
            extrude(context, id + "F5", {"entities" : qUnion([Q0]), "operationType" : NewBodyOperationType.ADD, "oppositeDirection" : true, "depth" : 3 * mm});
        }
        {
            var Q0;
            Q0=makeQuery(id+"F1.opExtrude","CAP_FACE",FACE,{"disambiguationData":[OSD([sQuery(id+"F0.wireOp",EDGE,"E168"),sQuery(id+"F0.wireOp",EDGE,"E169"),sQuery(id+"F0.wireOp",EDGE,"E170"),sQuery(id+"F0.wireOp",EDGE,"E171"),sQuery(id+"F0.wireOp",EDGE,"E172"),sQuery(id+"F0.wireOp",EDGE,"E173"),sQuery(id+"F0.wireOp",EDGE,"E174"),sQuery(id+"F0.wireOp",EDGE,"E175"),sQuery(id+"F0.wireOp",EDGE,"E176"),sQuery(id+"F0.wireOp",EDGE,"E177"),sQuery(id+"F0.wireOp",EDGE,"E178"),sQuery(id+"F0.wireOp",EDGE,"E179"),sQuery(id+"F0.wireOp",EDGE,"E180"),sQuery(id+"F0.wireOp",EDGE,"E181"),sQuery(id+"F0.wireOp",EDGE,"E182"),sQuery(id+"F0.wireOp",EDGE,"E183"),sQuery(id+"F0.wireOp",EDGE,"E184"),sQuery(id+"F0.wireOp",EDGE,"E185"),sQuery(id+"F0.wireOp",EDGE,"E186"),sQuery(id+"F0.wireOp",EDGE,"E187"),sQuery(id+"F0.wireOp",EDGE,"E188"),sQuery(id+"F0.wireOp",EDGE,"E189"),sQuery(id+"F0.wireOp",EDGE,"E190"),sQuery(id+"F0.wireOp",EDGE,"E191"),sQuery(id+"F0.wireOp",EDGE,"E192"),sQuery(id+"F0.wireOp",EDGE,"E193"),sQuery(id+"F0.wireOp",EDGE,"E194"),sQuery(id+"F0.wireOp",EDGE,"E195"),sQuery(id+"F0.wireOp",EDGE,"E196"),sQuery(id+"F0.wireOp",EDGE,"E197"),sQuery(id+"F0.wireOp",EDGE,"E198"),sQuery(id+"F0.wireOp",EDGE,"E199"),sQuery(id+"F0.wireOp",EDGE,"E200"),sQuery(id+"F0.wireOp",EDGE,"E201"),sQuery(id+"F0.wireOp",EDGE,"E202"),sQuery(id+"F0.wireOp",EDGE,"E203"),sQuery(id+"F0.wireOp",EDGE,"E204"),sQuery(id+"F0.wireOp",EDGE,"E205"),sQuery(id+"F0.wireOp",EDGE,"E206"),sQuery(id+"F0.wireOp",EDGE,"E207"),sQuery(id+"F0.wireOp",EDGE,"E208"),sQuery(id+"F0.wireOp",EDGE,"E209"),sQuery(id+"F0.wireOp",EDGE,"E210"),sQuery(id+"F0.wireOp",EDGE,"E211"),sQuery(id+"F0.wireOp",EDGE,"E212"),sQuery(id+"F0.wireOp",EDGE,"E213"),sQuery(id+"F0.wireOp",EDGE,"E214"),sQuery(id+"F0.wireOp",EDGE,"E215"),sQuery(id+"F0.wireOp",EDGE,"E216"),sQuery(id+"F0.wireOp",EDGE,"E217"),sQuery(id+"F0.wireOp",EDGE,"E218"),sQuery(id+"F0.wireOp",EDGE,"E219"),sQuery(id+"F0.wireOp",EDGE,"E220"),sQuery(id+"F0.wireOp",EDGE,"E221"),sQuery(id+"F0.wireOp",EDGE,"E222"),sQuery(id+"F0.wireOp",EDGE,"E223"),sQuery(id+"F0.wireOp",EDGE,"E224"),sQuery(id+"F0.wireOp",EDGE,"E225"),sQuery(id+"F0.wireOp",EDGE,"E226"),sQuery(id+"F0.wireOp",EDGE,"E227"),sQuery(id+"F0.wireOp",EDGE,"E228"),sQuery(id+"F0.wireOp",EDGE,"E229"),sQuery(id+"F0.wireOp",EDGE,"E230"),sQuery(id+"F0.wireOp",EDGE,"E231"),sQuery(id+"F0.wireOp",EDGE,"E232"),sQuery(id+"F0.wireOp",EDGE,"E233"),sQuery(id+"F0.wireOp",EDGE,"E234"),sQuery(id+"F0.wireOp",EDGE,"E235"),sQuery(id+"F0.wireOp",EDGE,"E236"),sQuery(id+"F0.wireOp",EDGE,"E237"),sQuery(id+"F0.wireOp",EDGE,"E238"),sQuery(id+"F0.wireOp",EDGE,"E239"),sQuery(id+"F0.wireOp",EDGE,"E240"),sQuery(id+"F0.wireOp",EDGE,"E241"),sQuery(id+"F0.wireOp",EDGE,"E242"),sQuery(id+"F0.wireOp",EDGE,"E243"),sQuery(id+"F0.wireOp",EDGE,"E244"),sQuery(id+"F0.wireOp",EDGE,"E245"),sQuery(id+"F0.wireOp",EDGE,"E246"),sQuery(id+"F0.wireOp",EDGE,"E247"),sQuery(id+"F0.wireOp",EDGE,"E248"),sQuery(id+"F0.wireOp",EDGE,"E249"),sQuery(id+"F0.wireOp",EDGE,"E250"),sQuery(id+"F0.wireOp",EDGE,"E251"),sQuery(id+"F0.wireOp",EDGE,"E252"),sQuery(id+"F0.wireOp",EDGE,"E253"),sQuery(id+"F0.wireOp",EDGE,"E254"),sQuery(id+"F0.wireOp",EDGE,"E255"),sQuery(id+"F0.wireOp",EDGE,"E256"),sQuery(id+"F0.wireOp",EDGE,"E257"),sQuery(id+"F0.wireOp",EDGE,"E258"),sQuery(id+"F0.wireOp",EDGE,"E259"),sQuery(id+"F0.wireOp",EDGE,"E260"),sQuery(id+"F0.wireOp",EDGE,"E261"),sQuery(id+"F0.wireOp",EDGE,"E262"),sQuery(id+"F0.wireOp",EDGE,"E263"),sQuery(id+"F0.wireOp",EDGE,"E264"),sQuery(id+"F0.wireOp",EDGE,"E265"),sQuery(id+"F0.wireOp",EDGE,"E266"),sQuery(id+"F0.wireOp",EDGE,"E267")])],"isStart":false});
            var sketch = newSketch(context, id + "F6", { "sketchPlane" : qUnion([Q0])});
            skLineSegment(sketch, "E270.bottom", {"start": v(555.27, 233.6) * mm, "end": v(575.27, 233.6) * mm});
            skLineSegment(sketch, "E270.left", {"start": v(555.27, 233.6) * mm, "end": v(555.27, 206.6) * mm});
            skLineSegment(sketch, "E270.right", {"start": v(852.27, 233.6) * mm, "end": v(852.27, 89.6) * mm});
            skLineSegment(sketch, "E271", {"start": v(-505.3, 191.6) * mm, "end": v(-208.3, 191.6) * mm, "construction": true});
            skLineSegment(sketch, "E272.bottom", {"start": v(555.27, 206.6) * mm, "end": v(552.27, 206.6) * mm});
            skLineSegment(sketch, "E272.top", {"start": v(555.27, 176.6) * mm, "end": v(552.27, 176.6) * mm});
            skLineSegment(sketch, "E272.right", {"start": v(552.27, 206.6) * mm, "end": v(552.27, 176.6) * mm});
            skLineSegment(sketch, "E273.bottom", {"start": v(555.27, 146.6) * mm, "end": v(552.27, 146.6) * mm});
            skLineSegment(sketch, "E273.top", {"start": v(555.27, 116.6) * mm, "end": v(552.27, 116.6) * mm});
            skLineSegment(sketch, "E273.right", {"start": v(552.27, 146.6) * mm, "end": v(552.27, 116.6) * mm});
            skLineSegment(sketch, "E274.trimOffspring", {"start": v(555.27, 116.6) * mm, "end": v(555.27, 89.6) * mm});
            skLineSegment(sketch, "E275.trimOffspring", {"start": v(555.27, 176.6) * mm, "end": v(555.27, 146.6) * mm});
            skLineSegment(sketch, "E276.top", {"start": v(575.27, 236.6) * mm, "end": v(605.27, 236.6) * mm});
            skLineSegment(sketch, "E276.left", {"start": v(575.27, 233.6) * mm, "end": v(575.27, 236.6) * mm});
            skLineSegment(sketch, "E276.right", {"start": v(605.27, 233.6) * mm, "end": v(605.27, 236.6) * mm});
            skLineSegment(sketch, "E277.trimOffspring", {"start": v(605.27, 233.6) * mm, "end": v(635.27, 233.6) * mm});
            skLineSegment(sketch, "E278.1.0.0", {"start": v(665.27, 233.6) * mm, "end": v(665.27, 236.6) * mm});
            skLineSegment(sketch, "E278.1.0.1", {"start": v(635.27, 233.6) * mm, "end": v(635.27, 236.6) * mm});
            skLineSegment(sketch, "E278.1.0.2", {"start": v(635.27, 236.6) * mm, "end": v(665.27, 236.6) * mm});
            skLineSegment(sketch, "E278.2.0.0", {"start": v(725.27, 233.6) * mm, "end": v(725.27, 236.6) * mm});
            skLineSegment(sketch, "E278.2.0.1", {"start": v(695.27, 233.6) * mm, "end": v(695.27, 236.6) * mm});
            skLineSegment(sketch, "E278.2.0.2", {"start": v(695.27, 236.6) * mm, "end": v(725.27, 236.6) * mm});
            skLineSegment(sketch, "E278.3.0.0", {"start": v(785.27, 233.6) * mm, "end": v(785.27, 236.6) * mm});
            skLineSegment(sketch, "E278.3.0.1", {"start": v(755.27, 233.6) * mm, "end": v(755.27, 236.6) * mm});
            skLineSegment(sketch, "E278.3.0.2", {"start": v(755.27, 236.6) * mm, "end": v(785.27, 236.6) * mm});
            skLineSegment(sketch, "E278.4.0.0", {"start": v(845.27, 233.6) * mm, "end": v(845.27, 236.6) * mm});
            skLineSegment(sketch, "E278.4.0.1", {"start": v(815.27, 233.6) * mm, "end": v(815.27, 236.6) * mm});
            skLineSegment(sketch, "E278.4.0.2", {"start": v(815.27, 236.6) * mm, "end": v(845.27, 236.6) * mm});
            skLineSegment(sketch, "E278.direction1", {"start": v(575.27, 233.6) * mm, "end": v(635.27, 233.6) * mm, "construction": true});
            skLineSegment(sketch, "E279.trimOffspring", {"start": v(665.27, 233.6) * mm, "end": v(695.27, 233.6) * mm});
            skLineSegment(sketch, "E280.trimOffspring", {"start": v(725.27, 233.6) * mm, "end": v(755.27, 233.6) * mm});
            skLineSegment(sketch, "E281.trimOffspring", {"start": v(785.27, 233.6) * mm, "end": v(815.27, 233.6) * mm});
            skLineSegment(sketch, "E282.trimOffspring", {"start": v(845.27, 233.6) * mm, "end": v(852.27, 233.6) * mm});
            skLineSegment(sketch, "E283", {"start": v(555.27, 161.6) * mm, "end": v(852.27, 161.6) * mm, "construction": true});
            skLineSegment(sketch, "E284.MirrorCS", {"start": v(845.27, 89.6) * mm, "end": v(852.27, 89.6) * mm});
            skLineSegment(sketch, "E285.MirrorCS", {"start": v(635.27, 89.6) * mm, "end": v(635.27, 86.6) * mm});
            skLineSegment(sketch, "E286.MirrorCS", {"start": v(575.27, 89.6) * mm, "end": v(575.27, 86.6) * mm});
            skLineSegment(sketch, "E287.MirrorCS", {"start": v(845.27, 89.6) * mm, "end": v(845.27, 86.6) * mm});
            skLineSegment(sketch, "E288.MirrorCS", {"start": v(755.27, 89.6) * mm, "end": v(755.27, 86.6) * mm});
            skLineSegment(sketch, "E289.MirrorCS", {"start": v(815.27, 89.6) * mm, "end": v(815.27, 86.6) * mm});
            skLineSegment(sketch, "E290.MirrorCS", {"start": v(785.27, 89.6) * mm, "end": v(785.27, 86.6) * mm});
            skLineSegment(sketch, "E291.MirrorCS", {"start": v(665.27, 89.6) * mm, "end": v(665.27, 86.6) * mm});
            skLineSegment(sketch, "E292.MirrorCS", {"start": v(695.27, 89.6) * mm, "end": v(695.27, 86.6) * mm});
            skLineSegment(sketch, "E293.MirrorCS", {"start": v(605.27, 89.6) * mm, "end": v(605.27, 86.6) * mm});
            skLineSegment(sketch, "E294.MirrorCS", {"start": v(725.27, 89.6) * mm, "end": v(725.27, 86.6) * mm});
            skLineSegment(sketch, "E295.MirrorCS", {"start": v(605.27, 89.6) * mm, "end": v(635.27, 89.6) * mm});
            skLineSegment(sketch, "E296.MirrorCS", {"start": v(555.27, 89.6) * mm, "end": v(575.27, 89.6) * mm});
            skLineSegment(sketch, "E297.MirrorCS", {"start": v(665.27, 89.6) * mm, "end": v(695.27, 89.6) * mm});
            skLineSegment(sketch, "E298.MirrorCS", {"start": v(785.27, 89.6) * mm, "end": v(815.27, 89.6) * mm});
            skLineSegment(sketch, "E299.MirrorCS", {"start": v(725.27, 89.6) * mm, "end": v(755.27, 89.6) * mm});
            skLineSegment(sketch, "E300.MirrorCS", {"start": v(755.27, 86.6) * mm, "end": v(785.27, 86.6) * mm});
            skLineSegment(sketch, "E301.MirrorCS", {"start": v(695.27, 86.6) * mm, "end": v(725.27, 86.6) * mm});
            skLineSegment(sketch, "E302.MirrorCS", {"start": v(635.27, 86.6) * mm, "end": v(665.27, 86.6) * mm});
            skLineSegment(sketch, "E303.MirrorCS", {"start": v(815.27, 86.6) * mm, "end": v(845.27, 86.6) * mm});
            skLineSegment(sketch, "E304.MirrorCS", {"start": v(575.27, 86.6) * mm, "end": v(605.27, 86.6) * mm});
            skSolve(sketch);
        }
        {
            var Q0;
            Q0 = qSketchRegion(id + "F6", true);
            extrude(context, id + "F7", {"entities" : qUnion([Q0]), "oppositeDirection" : true, "depth" : 3 * mm});
        }
        {
            var Q0;
            Q0=makeQuery(id+"F1.opExtrude","CAP_FACE",FACE,{"disambiguationData":[OSD([sQuery(id+"F0.wireOp",EDGE,"E168"),sQuery(id+"F0.wireOp",EDGE,"E169"),sQuery(id+"F0.wireOp",EDGE,"E170"),sQuery(id+"F0.wireOp",EDGE,"E171"),sQuery(id+"F0.wireOp",EDGE,"E172"),sQuery(id+"F0.wireOp",EDGE,"E173"),sQuery(id+"F0.wireOp",EDGE,"E174"),sQuery(id+"F0.wireOp",EDGE,"E175"),sQuery(id+"F0.wireOp",EDGE,"E176"),sQuery(id+"F0.wireOp",EDGE,"E177"),sQuery(id+"F0.wireOp",EDGE,"E178"),sQuery(id+"F0.wireOp",EDGE,"E179"),sQuery(id+"F0.wireOp",EDGE,"E180"),sQuery(id+"F0.wireOp",EDGE,"E181"),sQuery(id+"F0.wireOp",EDGE,"E182"),sQuery(id+"F0.wireOp",EDGE,"E183"),sQuery(id+"F0.wireOp",EDGE,"E184"),sQuery(id+"F0.wireOp",EDGE,"E185"),sQuery(id+"F0.wireOp",EDGE,"E186"),sQuery(id+"F0.wireOp",EDGE,"E187"),sQuery(id+"F0.wireOp",EDGE,"E188"),sQuery(id+"F0.wireOp",EDGE,"E189"),sQuery(id+"F0.wireOp",EDGE,"E190"),sQuery(id+"F0.wireOp",EDGE,"E191"),sQuery(id+"F0.wireOp",EDGE,"E192"),sQuery(id+"F0.wireOp",EDGE,"E193"),sQuery(id+"F0.wireOp",EDGE,"E194"),sQuery(id+"F0.wireOp",EDGE,"E195"),sQuery(id+"F0.wireOp",EDGE,"E196"),sQuery(id+"F0.wireOp",EDGE,"E197"),sQuery(id+"F0.wireOp",EDGE,"E198"),sQuery(id+"F0.wireOp",EDGE,"E199"),sQuery(id+"F0.wireOp",EDGE,"E200"),sQuery(id+"F0.wireOp",EDGE,"E201"),sQuery(id+"F0.wireOp",EDGE,"E202"),sQuery(id+"F0.wireOp",EDGE,"E203"),sQuery(id+"F0.wireOp",EDGE,"E204"),sQuery(id+"F0.wireOp",EDGE,"E205"),sQuery(id+"F0.wireOp",EDGE,"E206"),sQuery(id+"F0.wireOp",EDGE,"E207"),sQuery(id+"F0.wireOp",EDGE,"E208"),sQuery(id+"F0.wireOp",EDGE,"E209"),sQuery(id+"F0.wireOp",EDGE,"E210"),sQuery(id+"F0.wireOp",EDGE,"E211"),sQuery(id+"F0.wireOp",EDGE,"E212"),sQuery(id+"F0.wireOp",EDGE,"E213"),sQuery(id+"F0.wireOp",EDGE,"E214"),sQuery(id+"F0.wireOp",EDGE,"E215"),sQuery(id+"F0.wireOp",EDGE,"E216"),sQuery(id+"F0.wireOp",EDGE,"E217"),sQuery(id+"F0.wireOp",EDGE,"E218"),sQuery(id+"F0.wireOp",EDGE,"E219"),sQuery(id+"F0.wireOp",EDGE,"E220"),sQuery(id+"F0.wireOp",EDGE,"E221"),sQuery(id+"F0.wireOp",EDGE,"E222"),sQuery(id+"F0.wireOp",EDGE,"E223"),sQuery(id+"F0.wireOp",EDGE,"E224"),sQuery(id+"F0.wireOp",EDGE,"E225"),sQuery(id+"F0.wireOp",EDGE,"E226"),sQuery(id+"F0.wireOp",EDGE,"E227"),sQuery(id+"F0.wireOp",EDGE,"E228"),sQuery(id+"F0.wireOp",EDGE,"E229"),sQuery(id+"F0.wireOp",EDGE,"E230"),sQuery(id+"F0.wireOp",EDGE,"E231"),sQuery(id+"F0.wireOp",EDGE,"E232"),sQuery(id+"F0.wireOp",EDGE,"E233"),sQuery(id+"F0.wireOp",EDGE,"E234"),sQuery(id+"F0.wireOp",EDGE,"E235"),sQuery(id+"F0.wireOp",EDGE,"E236"),sQuery(id+"F0.wireOp",EDGE,"E237"),sQuery(id+"F0.wireOp",EDGE,"E238"),sQuery(id+"F0.wireOp",EDGE,"E239"),sQuery(id+"F0.wireOp",EDGE,"E240"),sQuery(id+"F0.wireOp",EDGE,"E241"),sQuery(id+"F0.wireOp",EDGE,"E242"),sQuery(id+"F0.wireOp",EDGE,"E243"),sQuery(id+"F0.wireOp",EDGE,"E244"),sQuery(id+"F0.wireOp",EDGE,"E245"),sQuery(id+"F0.wireOp",EDGE,"E246"),sQuery(id+"F0.wireOp",EDGE,"E247"),sQuery(id+"F0.wireOp",EDGE,"E248"),sQuery(id+"F0.wireOp",EDGE,"E249"),sQuery(id+"F0.wireOp",EDGE,"E250"),sQuery(id+"F0.wireOp",EDGE,"E251"),sQuery(id+"F0.wireOp",EDGE,"E252"),sQuery(id+"F0.wireOp",EDGE,"E253"),sQuery(id+"F0.wireOp",EDGE,"E254"),sQuery(id+"F0.wireOp",EDGE,"E255"),sQuery(id+"F0.wireOp",EDGE,"E256"),sQuery(id+"F0.wireOp",EDGE,"E257"),sQuery(id+"F0.wireOp",EDGE,"E258"),sQuery(id+"F0.wireOp",EDGE,"E259"),sQuery(id+"F0.wireOp",EDGE,"E260"),sQuery(id+"F0.wireOp",EDGE,"E261"),sQuery(id+"F0.wireOp",EDGE,"E262"),sQuery(id+"F0.wireOp",EDGE,"E263"),sQuery(id+"F0.wireOp",EDGE,"E264"),sQuery(id+"F0.wireOp",EDGE,"E265"),sQuery(id+"F0.wireOp",EDGE,"E266"),sQuery(id+"F0.wireOp",EDGE,"E267")])],"isStart":false});
            var sketch = newSketch(context, id + "F8", { "sketchPlane" : qUnion([Q0])});
            skLineSegment(sketch, "E305.bottom", {"start": v(-41.7, 206.6) * mm, "end": v(-38.7, 206.6) * mm});
            skLineSegment(sketch, "E305.top", {"start": v(-41.7, 176.6) * mm, "end": v(-38.7, 176.6) * mm});
            skLineSegment(sketch, "E305.left", {"start": v(-41.7, 206.6) * mm, "end": v(-41.7, 176.6) * mm});
            skLineSegment(sketch, "E305.right", {"start": v(-38.7, 206.6) * mm, "end": v(-38.7, 176.6) * mm});
            skLineSegment(sketch, "E306.bottom", {"start": v(-41.7, 146.6) * mm, "end": v(-38.7, 146.6) * mm});
            skLineSegment(sketch, "E306.top", {"start": v(-41.7, 116.6) * mm, "end": v(-38.7, 116.6) * mm});
            skLineSegment(sketch, "E306.left", {"start": v(-41.7, 146.6) * mm, "end": v(-41.7, 116.6) * mm});
            skLineSegment(sketch, "E306.right", {"start": v(-38.7, 146.6) * mm, "end": v(-38.7, 116.6) * mm});
            skLineSegment(sketch, "E307.bottom", {"start": v(-41.7, 40.4) * mm, "end": v(-38.7, 40.4) * mm});
            skLineSegment(sketch, "E307.top", {"start": v(-41.7, 10.4) * mm, "end": v(-38.7, 10.4) * mm});
            skLineSegment(sketch, "E307.left", {"start": v(-41.7, 40.4) * mm, "end": v(-41.7, 10.4) * mm});
            skLineSegment(sketch, "E307.right", {"start": v(-38.7, 40.4) * mm, "end": v(-38.7, 10.4) * mm});
            skLineSegment(sketch, "E308.bottom", {"start": v(-41.7, -19.6) * mm, "end": v(-38.7, -19.6) * mm});
            skLineSegment(sketch, "E308.top", {"start": v(-41.7, -49.6) * mm, "end": v(-38.7, -49.6) * mm});
            skLineSegment(sketch, "E308.left", {"start": v(-41.7, -19.6) * mm, "end": v(-41.7, -49.6) * mm});
            skLineSegment(sketch, "E308.right", {"start": v(-38.7, -19.6) * mm, "end": v(-38.7, -49.6) * mm});
            skLineSegment(sketch, "E309.bottom", {"start": v(-41.7, -79.6) * mm, "end": v(-38.7, -79.6) * mm});
            skLineSegment(sketch, "E309.top", {"start": v(-41.7, -109.6) * mm, "end": v(-38.7, -109.6) * mm});
            skLineSegment(sketch, "E309.left", {"start": v(-41.7, -79.6) * mm, "end": v(-41.7, -109.6) * mm});
            skLineSegment(sketch, "E309.right", {"start": v(-38.7, -79.6) * mm, "end": v(-38.7, -109.6) * mm});
            skLineSegment(sketch, "E310.bottom", {"start": v(-41.7, -139.6) * mm, "end": v(-38.7, -139.6) * mm});
            skLineSegment(sketch, "E310.top", {"start": v(-41.7, -169.6) * mm, "end": v(-38.7, -169.6) * mm});
            skLineSegment(sketch, "E310.left", {"start": v(-41.7, -139.6) * mm, "end": v(-41.7, -169.6) * mm});
            skLineSegment(sketch, "E310.right", {"start": v(-38.7, -139.6) * mm, "end": v(-38.7, -169.6) * mm});
            skLineSegment(sketch, "E311.bottom", {"start": v(-41.7, -199.6) * mm, "end": v(-38.7, -199.6) * mm});
            skLineSegment(sketch, "E311.top", {"start": v(-41.7, -229.6) * mm, "end": v(-38.7, -229.6) * mm});
            skLineSegment(sketch, "E311.left", {"start": v(-41.7, -199.6) * mm, "end": v(-41.7, -229.6) * mm});
            skLineSegment(sketch, "E311.right", {"start": v(-38.7, -199.6) * mm, "end": v(-38.7, -229.6) * mm});
            skLineSegment(sketch, "E312", {"start": v(-41.7, 40.4) * mm, "end": v(-41.7, 60.4) * mm, "construction": true});
            skLineSegment(sketch, "E313", {"start": v(-41.7, 10.4) * mm, "end": v(-41.7, -19.6) * mm, "construction": true});
            skLineSegment(sketch, "E314", {"start": v(-41.7, -49.6) * mm, "end": v(-41.7, -79.6) * mm, "construction": true});
            skLineSegment(sketch, "E315", {"start": v(-41.7, -109.6) * mm, "end": v(-41.7, -139.6) * mm, "construction": true});
            skLineSegment(sketch, "E316", {"start": v(-41.7, -169.6) * mm, "end": v(-41.7, -199.6) * mm, "construction": true});
            skLineSegment(sketch, "E317", {"start": v(36.3, -252.68) * mm, "end": v(36.3, -345.07) * mm, "construction": true});
            skLineSegment(sketch, "E318.MirrorCS", {"start": v(114.3, -199.6) * mm, "end": v(111.3, -199.6) * mm});
            skLineSegment(sketch, "E319.MirrorCS", {"start": v(114.3, -109.6) * mm, "end": v(111.3, -109.6) * mm});
            skLineSegment(sketch, "E320.MirrorCS", {"start": v(114.3, -49.6) * mm, "end": v(111.3, -49.6) * mm});
            skLineSegment(sketch, "E321.MirrorCS", {"start": v(114.3, -79.6) * mm, "end": v(111.3, -79.6) * mm});
            skLineSegment(sketch, "E322.MirrorCS", {"start": v(114.3, 40.4) * mm, "end": v(111.3, 40.4) * mm});
            skLineSegment(sketch, "E323.MirrorCS", {"start": v(114.3, 10.4) * mm, "end": v(111.3, 10.4) * mm});
            skLineSegment(sketch, "E324.MirrorCS", {"start": v(114.3, -169.6) * mm, "end": v(111.3, -169.6) * mm});
            skLineSegment(sketch, "E325.MirrorCS", {"start": v(114.3, -19.6) * mm, "end": v(111.3, -19.6) * mm});
            skLineSegment(sketch, "E326.MirrorCS", {"start": v(114.3, -139.6) * mm, "end": v(111.3, -139.6) * mm});
            skLineSegment(sketch, "E327.MirrorCS", {"start": v(114.3, 146.6) * mm, "end": v(111.3, 146.6) * mm});
            skLineSegment(sketch, "E328.MirrorCS", {"start": v(114.3, 116.6) * mm, "end": v(111.3, 116.6) * mm});
            skLineSegment(sketch, "E329.MirrorCS", {"start": v(114.3, -229.6) * mm, "end": v(111.3, -229.6) * mm});
            skLineSegment(sketch, "E330.MirrorCS", {"start": v(114.3, 206.6) * mm, "end": v(111.3, 206.6) * mm});
            skLineSegment(sketch, "E331.MirrorCS", {"start": v(114.3, 176.6) * mm, "end": v(111.3, 176.6) * mm});
            skLineSegment(sketch, "E332.MirrorCS", {"start": v(114.3, -79.6) * mm, "end": v(114.3, -109.6) * mm});
            skLineSegment(sketch, "E333.MirrorCS", {"start": v(114.3, 146.6) * mm, "end": v(114.3, 116.6) * mm});
            skLineSegment(sketch, "E334.MirrorCS", {"start": v(114.3, -139.6) * mm, "end": v(114.3, -169.6) * mm});
            skLineSegment(sketch, "E335.MirrorCS", {"start": v(114.3, -19.6) * mm, "end": v(114.3, -49.6) * mm});
            skLineSegment(sketch, "E336.MirrorCS", {"start": v(114.3, 40.4) * mm, "end": v(114.3, 60.4) * mm, "construction": true});
            skLineSegment(sketch, "E337.MirrorCS", {"start": v(114.3, 40.4) * mm, "end": v(114.3, 10.4) * mm});
            skLineSegment(sketch, "E338.MirrorCS", {"start": v(114.3, 206.6) * mm, "end": v(114.3, 176.6) * mm});
            skLineSegment(sketch, "E339.MirrorCS", {"start": v(114.3, -199.6) * mm, "end": v(114.3, -229.6) * mm});
            skLineSegment(sketch, "E340.MirrorCS", {"start": v(111.3, -139.6) * mm, "end": v(111.3, -169.6) * mm});
            skLineSegment(sketch, "E341.MirrorCS", {"start": v(114.3, -169.6) * mm, "end": v(114.3, -199.6) * mm, "construction": true});
            skLineSegment(sketch, "E342.MirrorCS", {"start": v(114.3, -109.6) * mm, "end": v(114.3, -139.6) * mm, "construction": true});
            skLineSegment(sketch, "E343.MirrorCS", {"start": v(111.3, -19.6) * mm, "end": v(111.3, -49.6) * mm});
            skLineSegment(sketch, "E344.MirrorCS", {"start": v(111.3, 146.6) * mm, "end": v(111.3, 116.6) * mm});
            skLineSegment(sketch, "E345.MirrorCS", {"start": v(114.3, 10.4) * mm, "end": v(114.3, -19.6) * mm, "construction": true});
            skLineSegment(sketch, "E346.MirrorCS", {"start": v(114.3, -49.6) * mm, "end": v(114.3, -79.6) * mm, "construction": true});
            skLineSegment(sketch, "E347.MirrorCS", {"start": v(111.3, 206.6) * mm, "end": v(111.3, 176.6) * mm});
            skLineSegment(sketch, "E348.MirrorCS", {"start": v(111.3, 40.4) * mm, "end": v(111.3, 10.4) * mm});
            skLineSegment(sketch, "E349.MirrorCS", {"start": v(111.3, -79.6) * mm, "end": v(111.3, -109.6) * mm});
            skLineSegment(sketch, "E350.MirrorCS", {"start": v(111.3, -199.6) * mm, "end": v(111.3, -229.6) * mm});
            skLineSegment(sketch, "E351", {"start": v(174.3, -253.95) * mm, "end": v(174.3, -307.25) * mm, "construction": true});
            skLineSegment(sketch, "E352.MirrorCS", {"start": v(234.3, -169.6) * mm, "end": v(237.3, -169.6) * mm});
            skLineSegment(sketch, "E353.MirrorCS", {"start": v(234.3, -199.6) * mm, "end": v(237.3, -199.6) * mm});
            skLineSegment(sketch, "E354.MirrorCS", {"start": v(234.3, -19.6) * mm, "end": v(237.3, -19.6) * mm});
            skLineSegment(sketch, "E355.MirrorCS", {"start": v(234.3, -139.6) * mm, "end": v(237.3, -139.6) * mm});
            skLineSegment(sketch, "E356.MirrorCS", {"start": v(234.3, -109.6) * mm, "end": v(237.3, -109.6) * mm});
            skLineSegment(sketch, "E357.MirrorCS", {"start": v(234.3, -49.6) * mm, "end": v(237.3, -49.6) * mm});
            skLineSegment(sketch, "E358.MirrorCS", {"start": v(234.3, 10.4) * mm, "end": v(237.3, 10.4) * mm});
            skLineSegment(sketch, "E359.MirrorCS", {"start": v(234.3, -79.6) * mm, "end": v(237.3, -79.6) * mm});
            skLineSegment(sketch, "E360.MirrorCS", {"start": v(234.3, 40.4) * mm, "end": v(237.3, 40.4) * mm});
            skLineSegment(sketch, "E361.MirrorCS", {"start": v(234.3, -229.6) * mm, "end": v(237.3, -229.6) * mm});
            skLineSegment(sketch, "E362.MirrorCS", {"start": v(237.3, -139.6) * mm, "end": v(237.3, -169.6) * mm});
            skLineSegment(sketch, "E363.MirrorCS", {"start": v(237.3, -199.6) * mm, "end": v(237.3, -229.6) * mm});
            skLineSegment(sketch, "E364.MirrorCS", {"start": v(234.3, -139.6) * mm, "end": v(234.3, -169.6) * mm});
            skLineSegment(sketch, "E365.MirrorCS", {"start": v(234.3, -169.6) * mm, "end": v(234.3, -199.6) * mm, "construction": true});
            skLineSegment(sketch, "E366.MirrorCS", {"start": v(234.3, -19.6) * mm, "end": v(234.3, -49.6) * mm});
            skLineSegment(sketch, "E367.MirrorCS", {"start": v(234.3, -109.6) * mm, "end": v(234.3, -139.6) * mm, "construction": true});
            skLineSegment(sketch, "E368.MirrorCS", {"start": v(237.3, -19.6) * mm, "end": v(237.3, -49.6) * mm});
            skLineSegment(sketch, "E369.MirrorCS", {"start": v(237.3, -79.6) * mm, "end": v(237.3, -109.6) * mm});
            skLineSegment(sketch, "E370.MirrorCS", {"start": v(234.3, -199.6) * mm, "end": v(234.3, -229.6) * mm});
            skLineSegment(sketch, "E371.MirrorCS", {"start": v(234.3, 10.4) * mm, "end": v(234.3, -19.6) * mm, "construction": true});
            skLineSegment(sketch, "E372.MirrorCS", {"start": v(234.3, -49.6) * mm, "end": v(234.3, -79.6) * mm, "construction": true});
            skLineSegment(sketch, "E373.MirrorCS", {"start": v(234.3, 40.4) * mm, "end": v(234.3, 60.4) * mm, "construction": true});
            skLineSegment(sketch, "E374.MirrorCS", {"start": v(234.3, -79.6) * mm, "end": v(234.3, -109.6) * mm});
            skLineSegment(sketch, "E375.MirrorCS", {"start": v(237.3, 40.4) * mm, "end": v(237.3, 10.4) * mm});
            skLineSegment(sketch, "E376.MirrorCS", {"start": v(234.3, 40.4) * mm, "end": v(234.3, 10.4) * mm});
            skLineSegment(sketch, "E377", {"start": v(297.3, -261.87) * mm, "end": v(297.3, -324.97) * mm, "construction": true});
            skLineSegment(sketch, "E378.MirrorCS", {"start": v(360.3, -109.6) * mm, "end": v(357.3, -109.6) * mm});
            skLineSegment(sketch, "E379.MirrorCS", {"start": v(360.3, -139.6) * mm, "end": v(357.3, -139.6) * mm});
            skLineSegment(sketch, "E380.MirrorCS", {"start": v(360.3, -19.6) * mm, "end": v(357.3, -19.6) * mm});
            skLineSegment(sketch, "E381.MirrorCS", {"start": v(360.3, -199.6) * mm, "end": v(357.3, -199.6) * mm});
            skLineSegment(sketch, "E382.MirrorCS", {"start": v(360.3, 40.4) * mm, "end": v(357.3, 40.4) * mm});
            skLineSegment(sketch, "E383.MirrorCS", {"start": v(360.3, -169.6) * mm, "end": v(357.3, -169.6) * mm});
            skLineSegment(sketch, "E384.MirrorCS", {"start": v(360.3, -79.6) * mm, "end": v(357.3, -79.6) * mm});
            skLineSegment(sketch, "E385.MirrorCS", {"start": v(360.3, 10.4) * mm, "end": v(357.3, 10.4) * mm});
            skLineSegment(sketch, "E386.MirrorCS", {"start": v(360.3, -49.6) * mm, "end": v(357.3, -49.6) * mm});
            skLineSegment(sketch, "E387.MirrorCS", {"start": v(360.3, -229.6) * mm, "end": v(357.3, -229.6) * mm});
            skLineSegment(sketch, "E388.MirrorCS", {"start": v(360.3, 40.4) * mm, "end": v(360.3, 60.4) * mm, "construction": true});
            skLineSegment(sketch, "E389.MirrorCS", {"start": v(360.3, -49.6) * mm, "end": v(360.3, -79.6) * mm, "construction": true});
            skLineSegment(sketch, "E390.MirrorCS", {"start": v(360.3, -169.6) * mm, "end": v(360.3, -199.6) * mm, "construction": true});
            skLineSegment(sketch, "E391.MirrorCS", {"start": v(360.3, -109.6) * mm, "end": v(360.3, -139.6) * mm, "construction": true});
            skLineSegment(sketch, "E392.MirrorCS", {"start": v(360.3, 10.4) * mm, "end": v(360.3, -19.6) * mm, "construction": true});
            skLineSegment(sketch, "E393.MirrorCS", {"start": v(360.3, -139.6) * mm, "end": v(360.3, -169.6) * mm});
            skLineSegment(sketch, "E394.MirrorCS", {"start": v(360.3, -199.6) * mm, "end": v(360.3, -229.6) * mm});
            skLineSegment(sketch, "E395.MirrorCS", {"start": v(357.3, -199.6) * mm, "end": v(357.3, -229.6) * mm});
            skLineSegment(sketch, "E396.MirrorCS", {"start": v(357.3, -79.6) * mm, "end": v(357.3, -109.6) * mm});
            skLineSegment(sketch, "E397.MirrorCS", {"start": v(357.3, -139.6) * mm, "end": v(357.3, -169.6) * mm});
            skLineSegment(sketch, "E398.MirrorCS", {"start": v(360.3, 40.4) * mm, "end": v(360.3, 10.4) * mm});
            skLineSegment(sketch, "E399.MirrorCS", {"start": v(357.3, -19.6) * mm, "end": v(357.3, -49.6) * mm});
            skLineSegment(sketch, "E400.MirrorCS", {"start": v(357.3, 40.4) * mm, "end": v(357.3, 10.4) * mm});
            skLineSegment(sketch, "E401.MirrorCS", {"start": v(360.3, -79.6) * mm, "end": v(360.3, -109.6) * mm});
            skLineSegment(sketch, "E402.MirrorCS", {"start": v(360.3, -19.6) * mm, "end": v(360.3, -49.6) * mm});
            skLineSegment(sketch, "E403.MirrorCS", {"start": v(234.3, 176.6) * mm, "end": v(237.3, 176.6) * mm});
            skLineSegment(sketch, "E404.MirrorCS", {"start": v(234.3, 206.6) * mm, "end": v(237.3, 206.6) * mm});
            skLineSegment(sketch, "E405.MirrorCS", {"start": v(234.3, 116.6) * mm, "end": v(237.3, 116.6) * mm});
            skLineSegment(sketch, "E406.MirrorCS", {"start": v(234.3, 146.6) * mm, "end": v(237.3, 146.6) * mm});
            skLineSegment(sketch, "E407.MirrorCS", {"start": v(234.3, 206.6) * mm, "end": v(234.3, 176.6) * mm});
            skLineSegment(sketch, "E408.MirrorCS", {"start": v(237.3, 146.6) * mm, "end": v(237.3, 116.6) * mm});
            skLineSegment(sketch, "E409.MirrorCS", {"start": v(237.3, 206.6) * mm, "end": v(237.3, 176.6) * mm});
            skLineSegment(sketch, "E410.MirrorCS", {"start": v(234.3, 146.6) * mm, "end": v(234.3, 116.6) * mm});
            skLineSegment(sketch, "E411.MirrorCS", {"start": v(360.3, 116.6) * mm, "end": v(357.3, 116.6) * mm});
            skLineSegment(sketch, "E412.MirrorCS", {"start": v(360.3, 206.6) * mm, "end": v(357.3, 206.6) * mm});
            skLineSegment(sketch, "E413.MirrorCS", {"start": v(360.3, 176.6) * mm, "end": v(357.3, 176.6) * mm});
            skLineSegment(sketch, "E414.MirrorCS", {"start": v(360.3, 146.6) * mm, "end": v(357.3, 146.6) * mm});
            skLineSegment(sketch, "E415.MirrorCS", {"start": v(360.3, 146.6) * mm, "end": v(360.3, 116.6) * mm});
            skLineSegment(sketch, "E416.MirrorCS", {"start": v(357.3, 146.6) * mm, "end": v(357.3, 116.6) * mm});
            skLineSegment(sketch, "E417.MirrorCS", {"start": v(357.3, 206.6) * mm, "end": v(357.3, 176.6) * mm});
            skLineSegment(sketch, "E418.MirrorCS", {"start": v(360.3, 206.6) * mm, "end": v(360.3, 176.6) * mm});
            skSolve(sketch);
        }
        {
            var Q0;
            Q0 = qSketchRegion(id + "F8", true);
            extrude(context, id + "F9", {"entities" : qUnion([Q0]), "operationType" : NewBodyOperationType.REMOVE, "endBound" : BoundingType.THROUGH_ALL, "oppositeDirection" : true, "depth" : 25 * mm});
        }
    });
